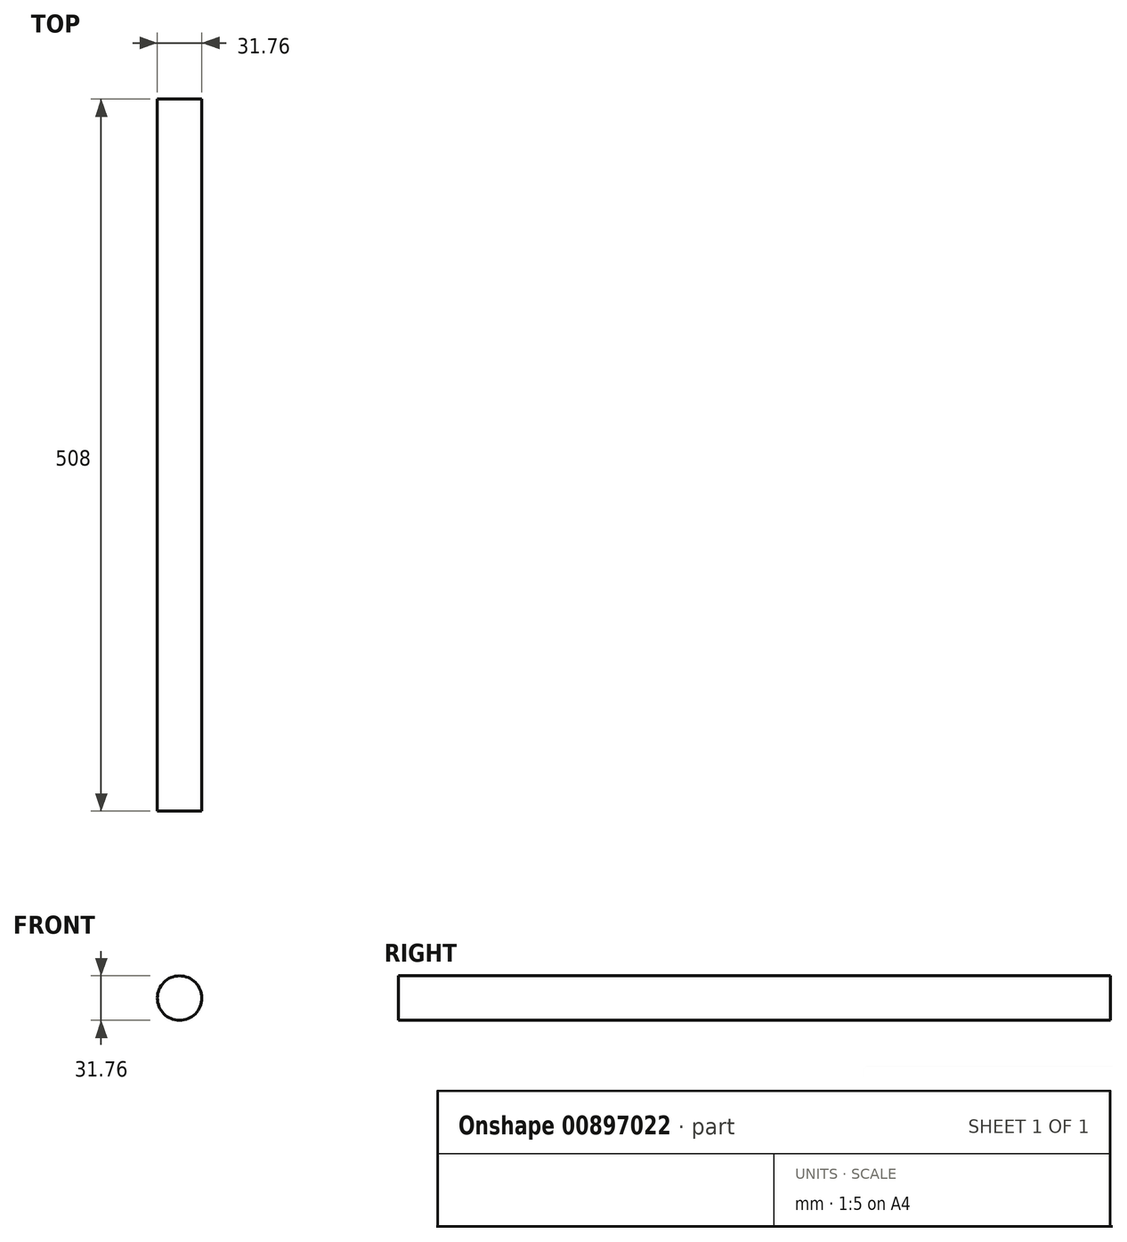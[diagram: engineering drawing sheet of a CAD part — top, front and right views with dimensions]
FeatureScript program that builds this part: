
annotation { "Feature Type Name" : "Feature", "Feature Type Description" : "" }
export const myFeature = defineFeature(function(context is Context, id is Id, definition is map)
    precondition{}
    {
        {
            var Q0;
            Q0=qCreatedBy(makeId("Front.planeOp"),FACE);
            var sketch = newSketch(context, id + "F0", { "sketchPlane" : qUnion([Q0])});
            skCircle(sketch, "E0", {"center": v(0, 0) * mm, "radius": 15.88 * mm});
            skSolve(sketch);
        }
        {
            var Q0;
            Q0 = qSketchRegion(id + "F0", true);
            extrude(context, id + "F1", {"entities" : qUnion([Q0]), "depth" : 508 * mm, "offsetDistance" : 25.4 * mm});
        }
    });
